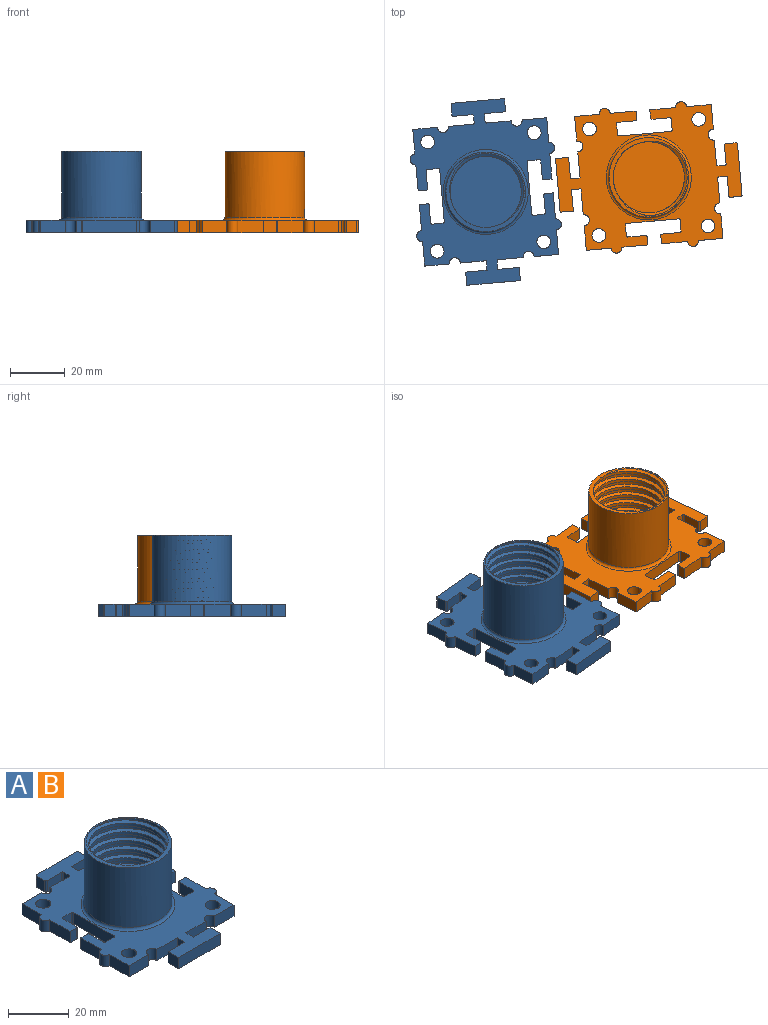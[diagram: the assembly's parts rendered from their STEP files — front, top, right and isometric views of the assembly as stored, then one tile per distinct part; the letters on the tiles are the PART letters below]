
ASSEMBLY  parts=2 mates=1
PART A: 86 faces, bbox 53.4x67.1x31.7 mm
  f0: plane 9x4.5mm, normal (0,1,0), area 40.5mm2, adj f2,f9,f63,f79
  f1: plane 9.5x4.5mm, normal (0,-1,0), area 42.8mm2, adj f2,f9,f60,f70
  f2: plane 66.6x52.95mm, normal (0,0,1), area 1596.3mm2, adj f0,f1,f3,f4,f5,f6,f7,f8
  f3: plane 9x4.5mm, normal (0,-1,0), area 40.5mm2, adj f2,f9,f11,f61
  f4: plane 9.5x4.5mm, normal (0,-1,0), area 42.8mm2, adj f2,f9,f61,f64
  f5: plane 9x4.5mm, normal (0,-1,0), area 40.5mm2, adj f2,f9,f16,f60
  f6: plane 9x4.5mm, normal (0,1,0), area 40.5mm2, adj f2,f9,f62,f78
  f7: plane 9x4.5mm, normal (0,1,0), area 40.5mm2, adj f2,f9,f12,f62
  f8: plane 9x4.5mm, normal (0,1,0), area 40.5mm2, adj f2,f9,f14,f63
  f9: plane 66.6x52.95mm, normal (0,0,-1), area 2351mm2, adj f0,f1,f3,f4,f5,f6,f7,f8
  f10: plane 9.5x4.5mm, normal (-1,0,0), area 42.8mm2, adj f2,f9,f36,f59
  f11: plane 9x4.5mm, normal (-1,0,0), area 40.5mm2, adj f2,f3,f9,f59
  f12: plane 9x4.5mm, normal (-1,0,0), area 40.5mm2, adj f2,f7,f9,f58
  f13: plane 9.5x4.5mm, normal (1,0,0), area 42.8mm2, adj f2,f9,f39,f57
  f14: plane 9x4.5mm, normal (1,0,0), area 40.5mm2, adj f2,f8,f9,f56
  f15: plane 9.5x4.5mm, normal (1,0,0), area 42.8mm2, adj f2,f9,f38,f56
  f16: plane 9x4.5mm, normal (1,0,0), area 40.5mm2, adj f2,f5,f9,f57
  f17: cylinder r=13mm len=26mm, axis (0,0,-1), area 678.2mm2, adj f18,f21,f22,f23
  f18: plane 29.39x29.39mm, normal (0,0,1), area 86.9mm2, adj f17,f19,f20,f21,f22
  f19: cylinder r=14.5mm len=29mm, axis (0,0,-1), area 2186.5mm2, adj f18,f25
  f20: cylinder r=14mm len=28mm, axis (0,0,-1), area 706.3mm2, adj f18,f21,f22,f23
  f21: bspline ~32.33x28mm, area 695.8mm2, adj f17,f18,f20,f23
  f22: bspline ~32.33x28mm, area 696.7mm2, adj f17,f18,f20,f23
  f23: plane 27.6x27.49mm, normal (0,0,1), area 573.6mm2, adj f17,f20,f21,f22
  f24: plane 9.5x4.5mm, normal (-1,0,0), area 42.8mm2, adj f2,f9,f30,f58
  f25: torus R=15.5mm, axis (0,0,-1), area 146.7mm2, adj f2,f19
  f26: cylinder r=2.5mm len=5mm, axis (0,0,1), area 70.7mm2, adj f2,f9
  f27: cylinder r=2.5mm len=5mm, axis (0,0,1), area 70.7mm2, adj f2,f9
  f28: cylinder r=2.5mm len=5mm, axis (0,0,1), area 70.7mm2, adj f2,f9
  f29: cylinder r=2.5mm len=5mm, axis (0,0,1), area 70.7mm2, adj f2,f9
  f30: plane 4.5x3mm, normal (0,-1,0), area 13.5mm2, adj f2,f9,f24,f44
  f31: plane 6.5x4.5mm, normal (1,0,0), area 29.3mm2, adj f2,f9,f44,f45
  f32: plane 4.5x4mm, normal (0,-1,0), area 18mm2, adj f2,f9,f45,f46
  f33: plane 19x4.5mm, normal (-1,0,0), area 85.5mm2, adj f2,f9,f46,f47
  f34: plane 4.5x4mm, normal (0,1,0), area 18mm2, adj f2,f9,f47,f48
  f35: plane 6.5x4.5mm, normal (1,0,0), area 29.3mm2, adj f2,f9,f48,f49
  f36: plane 4.5x3mm, normal (0,1,0), area 13.5mm2, adj f2,f9,f10,f49
  f37: plane 6.5x4.5mm, normal (-1,0,0), area 29.3mm2, adj f2,f9,f50,f55
  f38: plane 4.5x3mm, normal (0,-1,0), area 13.5mm2, adj f2,f9,f15,f55
  f39: plane 4.5x3mm, normal (0,1,0), area 13.5mm2, adj f2,f9,f13,f54
  f40: plane 6.5x4.5mm, normal (-1,0,0), area 29.3mm2, adj f2,f9,f53,f54
  f41: plane 4.5x4mm, normal (0,1,0), area 18mm2, adj f2,f9,f52,f53
  f42: plane 19x4.5mm, normal (1,0,0), area 85.5mm2, adj f2,f9,f51,f52
  f43: plane 4.5x4mm, normal (0,-1,0), area 18mm2, adj f2,f9,f50,f51
  f44: cylinder r=0.5mm len=4.5mm, axis (0,0,1), area 3.5mm2, adj f2,f9,f30,f31
  f45: cylinder r=0.5mm len=4.5mm, axis (0,0,-1), area 3.5mm2, adj f2,f9,f31,f32
  f46: cylinder r=0.5mm len=4.5mm, axis (0,0,1), area 3.5mm2, adj f2,f9,f32,f33
  f47: cylinder r=0.5mm len=4.5mm, axis (0,0,-1), area 3.5mm2, adj f2,f9,f33,f34
  f48: cylinder r=0.5mm len=4.5mm, axis (0,0,1), area 3.5mm2, adj f2,f9,f34,f35
  f49: cylinder r=0.5mm len=4.5mm, axis (0,0,-1), area 3.5mm2, adj f2,f9,f35,f36
  f50: cylinder r=0.5mm len=4.5mm, axis (0,0,-1), area 3.5mm2, adj f2,f9,f37,f43
  f51: cylinder r=0.5mm len=4.5mm, axis (0,0,1), area 3.5mm2, adj f2,f9,f42,f43
  f52: cylinder r=0.5mm len=4.5mm, axis (0,0,-1), area 3.5mm2, adj f2,f9,f41,f42
  f53: cylinder r=0.5mm len=4.5mm, axis (0,0,1), area 3.5mm2, adj f2,f9,f40,f41
  f54: cylinder r=0.5mm len=4.5mm, axis (0,0,-1), area 3.5mm2, adj f2,f9,f39,f40
  f55: cylinder r=0.5mm len=4.5mm, axis (0,0,1), area 3.5mm2, adj f2,f9,f37,f38
  f56: cylinder r=2mm len=4.5mm, axis (0,0,1), area 28mm2, adj f2,f9,f14,f15
  f57: cylinder r=2mm len=4.5mm, axis (0,0,1), area 28mm2, adj f2,f9,f13,f16
  f58: cylinder r=2mm len=4.5mm, axis (0,0,1), area 28mm2, adj f2,f9,f12,f24
  f59: cylinder r=2mm len=4.5mm, axis (0,0,1), area 28mm2, adj f2,f9,f10,f11
  f60: cylinder r=2mm len=4.5mm, axis (0,0,1), area 29mm2, adj f1,f2,f5,f9
  f61: cylinder r=2mm len=4.5mm, axis (0,0,1), area 29mm2, adj f2,f3,f4,f9
  f62: cylinder r=2mm len=4.5mm, axis (0,0,1), area 29mm2, adj f2,f6,f7,f9
  f63: cylinder r=2mm len=4.5mm, axis (0,0,1), area 29mm2, adj f0,f2,f8,f9
  f64: plane 4.5x3.5mm, normal (-1,0,0), area 15.8mm2, adj f2,f4,f9,f65
  f65: plane 7.8x4.5mm, normal (0,1,0), area 35.1mm2, adj f2,f9,f64,f66
  f66: plane 4.8x4.5mm, normal (-1,0,0), area 21.6mm2, adj f2,f9,f65,f67
  f67: plane 19.6x4.5mm, normal (0,-1,0), area 88.2mm2, adj f2,f9,f66,f68
  f68: plane 4.8x4.5mm, normal (1,0,0), area 21.6mm2, adj f2,f9,f67,f69
  f69: plane 7.8x4.5mm, normal (0,1,0), area 35.1mm2, adj f2,f9,f68,f70
  f70: plane 4.5x3.5mm, normal (1,0,0), area 15.8mm2, adj f1,f2,f9,f69
  f71: plane 4.5x2.5mm, normal (1,0,0), area 11.3mm2, adj f2,f9,f79,f80
  f72: plane 6.8x4.5mm, normal (0,-1,0), area 30.6mm2, adj f2,f9,f80,f81
  f73: plane 4.5x3.8mm, normal (1,0,0), area 17.1mm2, adj f2,f9,f81,f82
  f74: plane 18.6x4.5mm, normal (0,1,0), area 83.7mm2, adj f2,f9,f82,f83
  f75: plane 4.5x2.5mm, normal (-1,0,0), area 11.3mm2, adj f2,f9,f78,f84
  f76: plane 4.5x3.8mm, normal (-1,0,0), area 17.1mm2, adj f2,f9,f83,f85
  f77: plane 6.8x4.5mm, normal (0,-1,0), area 30.6mm2, adj f2,f9,f84,f85
  f78: cylinder r=0.5mm len=4.5mm, axis (0,0,1), area 3.5mm2, adj f2,f6,f9,f75
  f79: cylinder r=0.5mm len=4.5mm, axis (0,0,-1), area 3.5mm2, adj f0,f2,f9,f71
  f80: cylinder r=0.5mm len=4.5mm, axis (0,0,-1), area 3.5mm2, adj f2,f9,f71,f72
  f81: cylinder r=0.5mm len=4.5mm, axis (0,0,1), area 3.5mm2, adj f2,f9,f72,f73
  f82: cylinder r=0.5mm len=4.5mm, axis (0,0,-1), area 3.5mm2, adj f2,f9,f73,f74
  f83: cylinder r=0.5mm len=4.5mm, axis (0,0,1), area 3.5mm2, adj f2,f9,f74,f76
  f84: cylinder r=0.5mm len=4.5mm, axis (0,0,1), area 3.5mm2, adj f2,f9,f75,f77
  f85: cylinder r=0.5mm len=4.5mm, axis (0,0,-1), area 3.5mm2, adj f2,f9,f76,f77
PART B: same geometry as A
PLACE A rot(axis=(0,0,1),5deg) t=(-32.15,-26.79,-8.98)mm
PLACE B rot(axis=(0,0,-1),85deg) t=(27.32,-21.5,-9.02)mm
MATE parallel A.f42 <-> B.f67  axis (1,0.09,0) through (-16.21,-25.39,-21.48)mm
